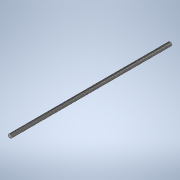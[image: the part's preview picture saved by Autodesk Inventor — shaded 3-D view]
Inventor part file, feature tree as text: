
AUTODESK INVENTOR PART (.ipt)
format: ipt  version: 2020 (Build 240168000, 168)  size: 749,568 bytes
history: native  units: mm
features: sketch x2, extrude x1, helix x1, pattern_circular x1
ambient origin geometry x8: Origin, YZ Plane, XZ Plane, XY Plane, X Axis, Y Axis, Z Axis, Center Point
bodies: Solid1 (feature_tree)
feature tree (5):
  extrude  "Extrusion1"  Depth=350.0mm TaperAngle=0.0deg
  helix  "Coil1"  [1 undecoded]
  pattern_circular  "Circular Pattern1"  Count=4 Angle=360.0deg
  sketch  "Sketch1"  dims[d0=8.0mm d1=350.0mm d2=0.0mm d3=1.0mm]
  sketch  "Sketch2"  dims[d4=3.8mm d5=8.0mm d6=10.0mm d7=437.5mm d8=0.0mm d9=90.0deg d10=90.0deg d11=0.0mm d12=0.0mm d13=40.0mm d14=360.0deg]
note: 1 required parameter value undecoded (feature->parameter linkage not recoverable at this tier; creation-order binding heuristic only, values carry confidence <= 0.55)
